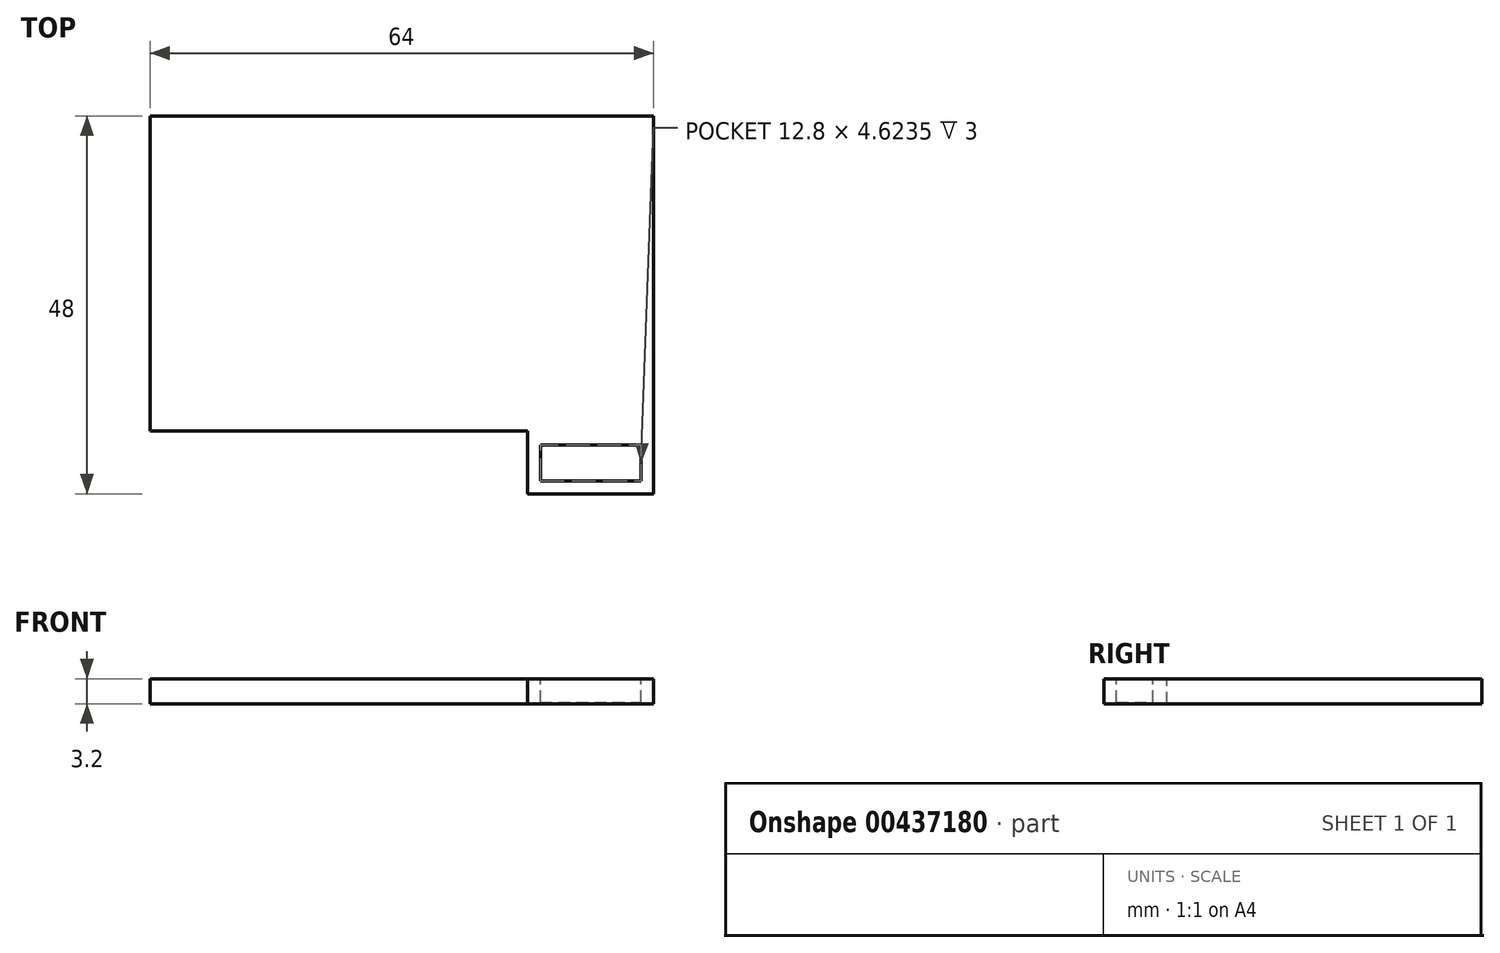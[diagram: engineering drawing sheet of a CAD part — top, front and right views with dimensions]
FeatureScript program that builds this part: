
annotation { "Feature Type Name" : "Feature", "Feature Type Description" : "" }
export const myFeature = defineFeature(function(context is Context, id is Id, definition is map)
    precondition{}
    {
        {
            var Q0;
            Q0=qCreatedBy(makeId("Top.planeOp"),FACE);
            var sketch = newSketch(context, id + "F0", { "sketchPlane" : qUnion([Q0])});
            skLineSegment(sketch, "E0.bottom", {"start": v(0, 0) * mm, "end": v(64, 0) * mm});
            skLineSegment(sketch, "E0.top", {"start": v(0, -40) * mm, "end": v(64, -40) * mm});
            skLineSegment(sketch, "E0.left", {"start": v(0, 0) * mm, "end": v(0, -40) * mm});
            skLineSegment(sketch, "E0.right", {"start": v(64, 0) * mm, "end": v(64, -40) * mm});
            skLineSegment(sketch, "E1.bottom", {"start": v(64, -40) * mm, "end": v(48, -40) * mm});
            skLineSegment(sketch, "E1.top", {"start": v(64, -48) * mm, "end": v(48, -48) * mm});
            skLineSegment(sketch, "E1.left", {"start": v(64, -40) * mm, "end": v(64, -48) * mm});
            skLineSegment(sketch, "E1.right", {"start": v(48, -40) * mm, "end": v(48, -48) * mm});
            skSolve(sketch);
        }
        {
            var Q0;
            Q0 = qSketchRegion(id + "F0", true);
            extrude(context, id + "F1", {"entities" : qUnion([Q0]), "oppositeDirection" : true, "depth" : 3.2 * mm});
        }
        {
            var Q0;
            Q0=makeQuery(id+"F1.opExtrude","CAP_FACE",FACE,{"disambiguationData":[OSD([sQuery(id+"F0.wireOp",EDGE,"E0.bottom"),sQuery(id+"F0.wireOp",EDGE,"E0.top"),sQuery(id+"F0.wireOp",EDGE,"E0.left"),sQuery(id+"F0.wireOp",EDGE,"E0.right"),sQuery(id+"F0.wireOp",EDGE,"E1.top"),sQuery(id+"F0.wireOp",EDGE,"E1.left"),sQuery(id+"F0.wireOp",EDGE,"E1.right")])],"isStart":true});
            var sketch = newSketch(context, id + "F2", { "sketchPlane" : qUnion([Q0])});
            skLineSegment(sketch, "E2", {"start": v(48, -44) * mm, "end": v(49.6, -44) * mm});
            skLineSegment(sketch, "E3", {"start": v(49.6, -48) * mm, "end": v(49.6, -46.4) * mm});
            skLineSegment(sketch, "E4.bottom", {"start": v(49.6, -46.4) * mm, "end": v(60.47, -46.4) * mm});
            skLineSegment(sketch, "E4.top", {"start": v(49.6, -41.78) * mm, "end": v(60.47, -41.78) * mm});
            skLineSegment(sketch, "E4.left", {"start": v(49.6, -46.4) * mm, "end": v(49.6, -41.78) * mm});
            skLineSegment(sketch, "E4.right", {"start": v(60.47, -46.4) * mm, "end": v(60.47, -41.78) * mm});
            skLineSegment(sketch, "E5", {"start": v(64, -43.72) * mm, "end": v(62.4, -43.72) * mm});
            skLineSegment(sketch, "E6.bottom", {"start": v(49.6, -41.78) * mm, "end": v(62.4, -41.78) * mm});
            skLineSegment(sketch, "E6.top", {"start": v(49.6, -46.4) * mm, "end": v(62.4, -46.4) * mm});
            skLineSegment(sketch, "E6.left", {"start": v(49.6, -41.78) * mm, "end": v(49.6, -46.4) * mm});
            skLineSegment(sketch, "E6.right", {"start": v(62.4, -41.78) * mm, "end": v(62.4, -46.4) * mm});
            skSolve(sketch);
        }
        {
            var Q0;
            Q0 = qSketchRegion(id + "F2", true);
            extrude(context, id + "F3", {"entities" : qUnion([Q0]), "operationType" : NewBodyOperationType.REMOVE, "oppositeDirection" : true, "depth" : 3 * mm});
        }
    });
